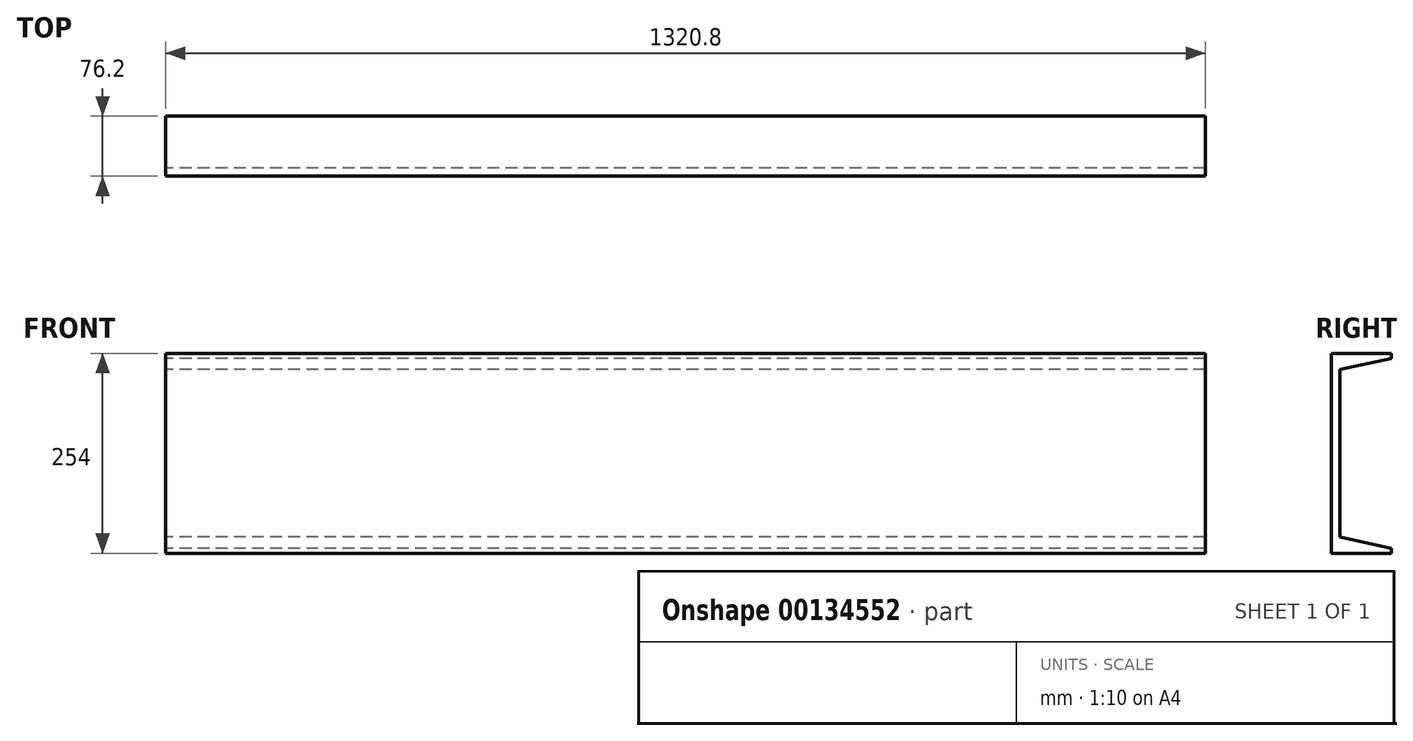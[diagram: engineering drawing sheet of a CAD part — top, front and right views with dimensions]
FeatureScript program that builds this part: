
annotation { "Feature Type Name" : "Feature", "Feature Type Description" : "" }
export const myFeature = defineFeature(function(context is Context, id is Id, definition is map)
    precondition{}
    {
        {
            var Q0;
            Q0=qCreatedBy(makeId("Right.planeOp"),FACE);
            var sketch = newSketch(context, id + "F0", { "sketchPlane" : qUnion([Q0])});
            skLineSegment(sketch, "E0", {"start": v(-28.27, 267) * mm, "end": v(-28.27, 13) * mm});
            skLineSegment(sketch, "E1", {"start": v(-28.27, 13) * mm, "end": v(47.93, 13) * mm});
            skLineSegment(sketch, "E2", {"start": v(47.93, 13) * mm, "end": v(47.93, 19.36) * mm});
            skLineSegment(sketch, "E3", {"start": v(47.93, 19.36) * mm, "end": v(-17.72, 33.68) * mm});
            skLineSegment(sketch, "E4", {"start": v(-28.27, 267) * mm, "end": v(47.93, 267) * mm});
            skLineSegment(sketch, "E5", {"start": v(47.93, 267) * mm, "end": v(47.93, 260.66) * mm});
            skLineSegment(sketch, "E6", {"start": v(-17.72, 246.33) * mm, "end": v(47.93, 260.66) * mm});
            skLineSegment(sketch, "E7", {"start": v(-17.72, 246.33) * mm, "end": v(-17.72, 33.68) * mm});
            skSolve(sketch);
        }
        {
            var Q0;
            Q0 = qSketchRegion(id + "F0", true);
            extrude(context, id + "F1", {"entities" : qUnion([Q0]), "depth" : 1320.8 * mm});
        }
    });
